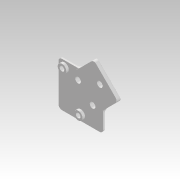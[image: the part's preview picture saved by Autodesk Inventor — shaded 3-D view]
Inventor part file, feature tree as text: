
AUTODESK INVENTOR PART (.ipt)
format: ipt  version: 2020 (Build 240168000, 168)  size: 388,608 bytes
history: native  units: mm
features: sketch x8, extrude x8, plane x2, fillet x2, projected_geometry x2, mirror x1
ambient origin geometry x8: Origin, YZ Plane, XZ Plane, XY Plane, X Axis, Y Axis, Z Axis, Center Point
bodies: Solid1 (feature_tree)
feature tree (23):
  sketch  "Sketch1"  dims[d0=26.0mm d1=26.0mm]
  extrude  "Extrusion1"  Depth=26.0mm
  plane  "Work Plane1"
  sketch  "Sketch3"  dims[d5=1.0mm d6=0.0mm d7=2.0mm]
  extrude  "Extrusion3"  Depth=2.7mm
  extrude  "Extrusion8"  Depth=2.0mm
  extrude  "Extrusion5"  Depth=1.5mm TaperAngle=0.0deg
  extrude  "Extrusion2"  Depth=15.0mm
  plane  "Work Plane2"
  extrude  "Extrusion6"  Depth=3.0mm
  extrude  "Extrusion7"  Depth=25.0mm
  extrude  "Extrusion9"  Depth=15.0mm TaperAngle=0.0deg
  mirror  "Mirror1"
  fillet  "Fillet1"  Radius=3.0mm
  fillet  "Fillet2"  Radius=2.0mm
  sketch  "Sketch2"  dims[d3=19.0mm d4=2.7mm]
  sketch  "Sketch4"  dims[d8=5.0mm d9=1.5mm d10=0.0mm]
  projected_geometry  "Projected Loop1"
  sketch  "Sketch6"  dims[d11=25.0mm d12=15.0mm]
  sketch  "Sketch7"  dims[d13=2.0mm d14=3.0mm]
  projected_geometry  "Projected Loop2"
  sketch  "Sketch8"  dims[d15=10.0mm d16=25.0mm]
  sketch  "Sketch9"  dims[d17=20.0mm d18=0.0mm d22=15.0mm d23=0.0mm d24=3.0mm d25=2.0mm d26=-3.0mm d29=4.0mm d30=4.0mm d31=3.3mm d32=3.0mm d33=0.0mm d34=6.0mm d35=3.0mm d36=0.0mm d37=10.0mm d38=12.0mm d39=12.0mm d40=25.0mm d41=19.0mm d42=6.659mm d43=0.0mm d44=12.0mm d45=12.0mm d46=4.0mm d47=1.5mm d48=0.0mm d49=10.0mm d50=10.0mm d51=5.0mm d52=1.5mm d53=0.5mm]
